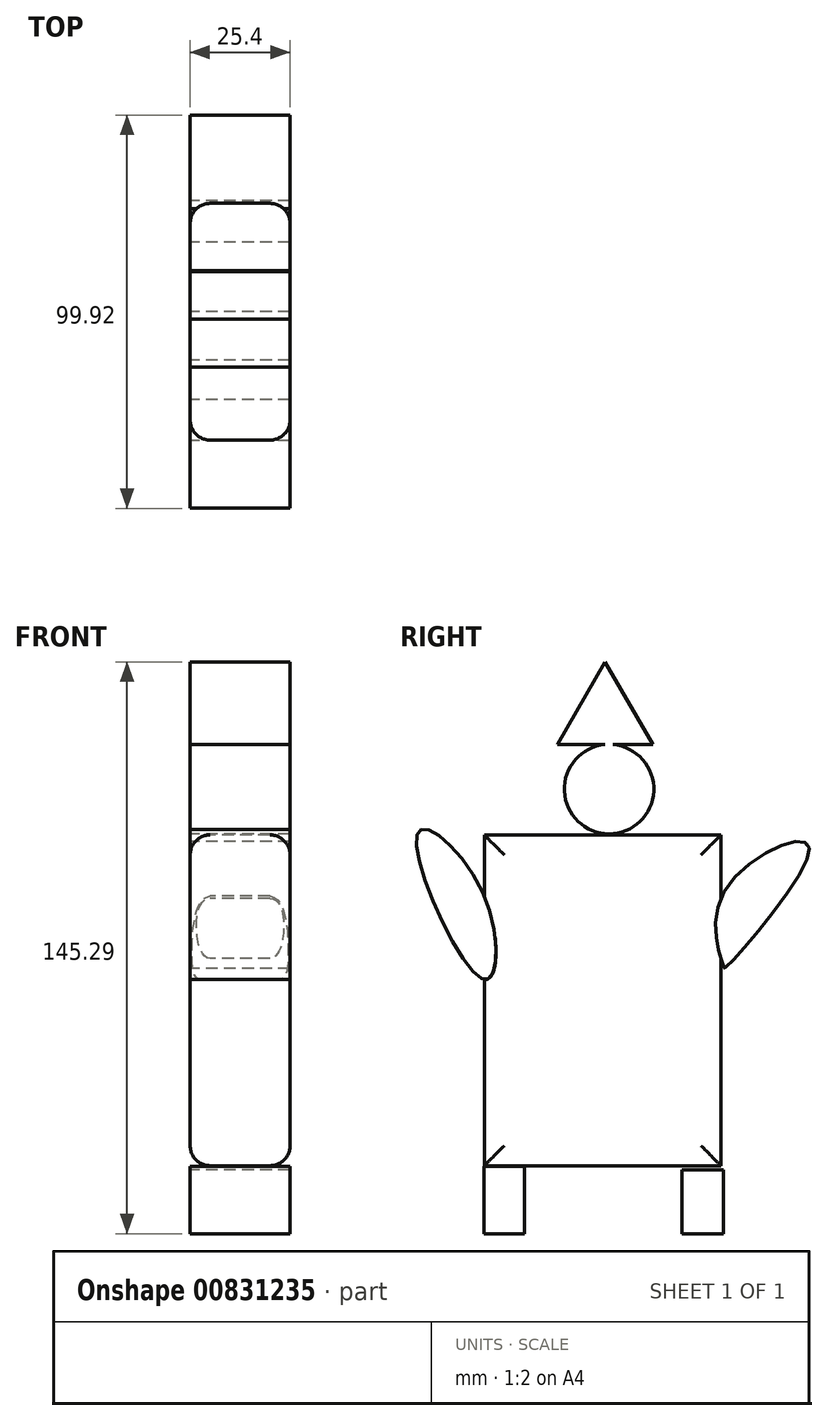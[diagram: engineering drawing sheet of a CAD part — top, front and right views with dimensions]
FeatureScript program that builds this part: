
annotation { "Feature Type Name" : "Feature", "Feature Type Description" : "" }
export const myFeature = defineFeature(function(context is Context, id is Id, definition is map)
    precondition{}
    {
        {
            var Q0;
            Q0=qCreatedBy(makeId("Right.planeOp"),FACE);
            var sketch = newSketch(context, id + "F0", { "sketchPlane" : qUnion([Q0])});
            skLineSegment(sketch, "E0.bottom", {"start": v(-28.86, 27.79) * mm, "end": v(31.28, 27.79) * mm});
            skLineSegment(sketch, "E0.top", {"start": v(-28.86, -56.25) * mm, "end": v(31.28, -56.25) * mm});
            skLineSegment(sketch, "E0.left", {"start": v(-28.86, 27.79) * mm, "end": v(-28.86, -56.25) * mm});
            skLineSegment(sketch, "E0.right", {"start": v(31.28, 27.79) * mm, "end": v(31.28, -56.25) * mm});
            skSolve(sketch);
        }
        {
            var Q0;
            Q0=makeQuery(id+"F0.imprint","IMPRINT",FACE,{"disambiguationData":[TD([[makeQuery(id+"F0.imprint","IMPRINT",EDGE,{"derivedFrom":sQuery(id+"F0.wireOp",EDGE,"E0.bottom")}),-1.0]])]});
            extrude(context, id + "F1", {"entities" : qUnion([Q0]), "depth" : 25.4 * mm, "offsetDistance" : 25.4 * mm});
        }
        {
            var Q0;
            Q0=makeQuery(id+"F1.opExtrude","CAP_EDGE",EDGE,{"disambiguationData":[OSD([sQuery(id+"F0.wireOp",EDGE,"E0.left")])],"isStart":false});
            var Q1;
            Q1=makeQuery(id+"F1.opExtrude","CAP_EDGE",EDGE,{"disambiguationData":[OSD([sQuery(id+"F0.wireOp",EDGE,"E0.right")])],"isStart":false});
            var Q2;
            Q2=makeQuery(id+"F1.opExtrude","CAP_EDGE",EDGE,{"disambiguationData":[OSD([sQuery(id+"F0.wireOp",EDGE,"E0.bottom")])],"isStart":false});
            var Q3;
            Q3=makeQuery(id+"F1.opExtrude","CAP_EDGE",EDGE,{"disambiguationData":[OSD([sQuery(id+"F0.wireOp",EDGE,"E0.top")])],"isStart":false});
            var Q4;
            Q4=makeQuery(id+"F1.opExtrude","CAP_EDGE",EDGE,{"disambiguationData":[OSD([sQuery(id+"F0.wireOp",EDGE,"E0.bottom")])],"isStart":true});
            var Q5;
            Q5=makeQuery(id+"F1.opExtrude","CAP_EDGE",EDGE,{"disambiguationData":[OSD([sQuery(id+"F0.wireOp",EDGE,"E0.top")])],"isStart":true});
            var Q6;
            Q6=makeQuery(id+"F1.opExtrude","CAP_EDGE",EDGE,{"disambiguationData":[OSD([sQuery(id+"F0.wireOp",EDGE,"E0.left")])],"isStart":true});
            var Q7;
            Q7=makeQuery(id+"F1.opExtrude","CAP_EDGE",EDGE,{"disambiguationData":[OSD([sQuery(id+"F0.wireOp",EDGE,"E0.right")])],"isStart":true});
            fillet(context, id + "F2", {"entities" : qUnion([Q0, Q1, Q2, Q3, Q4, Q5, Q6, Q7]), "radius" : 5.08 * mm, "tangentPropagation" : true, "allowEdgeOverflow" : false});
        }
        {
            var Q0;
            Q0=qCreatedBy(makeId("Right.planeOp"),FACE);
            var sketch = newSketch(context, id + "F3", { "sketchPlane" : qUnion([Q0])});
            skCircle(sketch, "E1", {"center": v(2.83, 39.42) * mm, "radius": 11.37 * mm});
            skPoint(sketch, "E1.first.point", {"position": v(1.83, 50.74) * mm});
            skPoint(sketch, "E1.second.point", {"position": v(3.31, 28.06) * mm});
            skPoint(sketch, "E1.third.point", {"position": v(11.42, 46.86) * mm});
            skFitSpline(sketch, "E2", {"points": [v(32.08, 13.3) * mm, v(53.66, 24.73) * mm, v(32.27, -6.06) * mm, v(32.09, -6.06) * mm, v(31.9, -5.5) * mm, v(32.08, 13.3) * mm]});
            skFitSpline(sketch, "E3", {"points": [v(-29.33, 13.3) * mm, v(-45.93, 28.07) * mm, v(-29.32, -8.81) * mm, v(-29.33, 13.3) * mm]});
            skLineSegment(sketch, "E4.bottom", {"start": v(-18.62, -56.38) * mm, "end": v(-28.94, -56.38) * mm});
            skLineSegment(sketch, "E4.top", {"start": v(-18.62, -73.53) * mm, "end": v(-28.94, -73.53) * mm});
            skLineSegment(sketch, "E4.left", {"start": v(-18.62, -56.38) * mm, "end": v(-18.62, -73.53) * mm});
            skLineSegment(sketch, "E4.right", {"start": v(-28.94, -56.38) * mm, "end": v(-28.94, -73.53) * mm});
            skLineSegment(sketch, "E5.bottom", {"start": v(31.92, -57.32) * mm, "end": v(21.4, -57.32) * mm});
            skLineSegment(sketch, "E5.top", {"start": v(31.92, -73.53) * mm, "end": v(21.4, -73.53) * mm});
            skLineSegment(sketch, "E5.left", {"start": v(31.92, -57.32) * mm, "end": v(31.92, -73.53) * mm});
            skLineSegment(sketch, "E5.right", {"start": v(21.4, -57.32) * mm, "end": v(21.4, -73.53) * mm});
            skCircle(sketch, "E6.cCircle", {"center": v(1.83, 57.74) * mm, "radius": 7 * mm, "construction": true});
            skLineSegment(sketch, "E6.0", {"start": v(13.96, 50.74) * mm, "end": v(-10.3, 50.73) * mm});
            skLineSegment(sketch, "E6.1", {"start": v(-10.3, 50.73) * mm, "end": v(1.82, 71.76) * mm});
            skLineSegment(sketch, "E6.2", {"start": v(1.82, 71.76) * mm, "end": v(13.96, 50.74) * mm});
            skCircle(sketch, "E7.cCircle", {"center": v(1.83, 50.74) * mm, "radius": 2 * mm, "construction": true});
            skLineSegment(sketch, "E7.0", {"start": v(3.83, 50.86) * mm, "end": v(3.83, 50.61) * mm, "construction": true});
            skLineSegment(sketch, "E7.1", {"start": v(3.83, 50.61) * mm, "end": v(3.8, 50.36) * mm, "construction": true});
            skLineSegment(sketch, "E7.2", {"start": v(3.8, 50.36) * mm, "end": v(3.74, 50.12) * mm, "construction": true});
            skLineSegment(sketch, "E7.3", {"start": v(3.74, 50.12) * mm, "end": v(3.65, 49.88) * mm, "construction": true});
            skLineSegment(sketch, "E7.4", {"start": v(3.65, 49.88) * mm, "end": v(3.52, 49.66) * mm, "construction": true});
            skLineSegment(sketch, "E7.5", {"start": v(3.52, 49.66) * mm, "end": v(3.38, 49.46) * mm, "construction": true});
            skLineSegment(sketch, "E7.6", {"start": v(3.38, 49.46) * mm, "end": v(3.2, 49.28) * mm, "construction": true});
            skLineSegment(sketch, "E7.7", {"start": v(3.2, 49.28) * mm, "end": v(3, 49.11) * mm, "construction": true});
            skLineSegment(sketch, "E7.8", {"start": v(3, 49.11) * mm, "end": v(2.8, 48.98) * mm, "construction": true});
            skLineSegment(sketch, "E7.9", {"start": v(2.8, 48.98) * mm, "end": v(2.57, 48.87) * mm, "construction": true});
            skLineSegment(sketch, "E7.10", {"start": v(2.57, 48.87) * mm, "end": v(2.33, 48.8) * mm, "construction": true});
            skLineSegment(sketch, "E7.11", {"start": v(2.33, 48.8) * mm, "end": v(2.08, 48.75) * mm, "construction": true});
            skLineSegment(sketch, "E7.12", {"start": v(2.08, 48.75) * mm, "end": v(1.83, 48.73) * mm, "construction": true});
            skLineSegment(sketch, "E7.13", {"start": v(1.83, 48.73) * mm, "end": v(1.58, 48.75) * mm, "construction": true});
            skLineSegment(sketch, "E7.14", {"start": v(1.58, 48.75) * mm, "end": v(1.33, 48.8) * mm, "construction": true});
            skLineSegment(sketch, "E7.15", {"start": v(1.33, 48.8) * mm, "end": v(1.1, 48.87) * mm, "construction": true});
            skLineSegment(sketch, "E7.16", {"start": v(1.1, 48.87) * mm, "end": v(0.86, 48.98) * mm, "construction": true});
            skLineSegment(sketch, "E7.17", {"start": v(0.86, 48.98) * mm, "end": v(0.65, 49.11) * mm, "construction": true});
            skLineSegment(sketch, "E7.18", {"start": v(0.65, 49.11) * mm, "end": v(0.46, 49.27) * mm, "construction": true});
            skLineSegment(sketch, "E7.19", {"start": v(0.46, 49.27) * mm, "end": v(0.28, 49.46) * mm, "construction": true});
            skLineSegment(sketch, "E7.20", {"start": v(0.28, 49.46) * mm, "end": v(0.14, 49.66) * mm, "construction": true});
            skLineSegment(sketch, "E7.21", {"start": v(0.14, 49.66) * mm, "end": v(0.01, 49.88) * mm, "construction": true});
            skLineSegment(sketch, "E7.22", {"start": v(0.01, 49.88) * mm, "end": v(-0.08, 50.12) * mm, "construction": true});
            skLineSegment(sketch, "E7.23", {"start": v(-0.08, 50.12) * mm, "end": v(-0.14, 50.36) * mm, "construction": true});
            skLineSegment(sketch, "E7.24", {"start": v(-0.14, 50.36) * mm, "end": v(-0.17, 50.61) * mm, "construction": true});
            skLineSegment(sketch, "E7.25", {"start": v(-0.17, 50.61) * mm, "end": v(-0.17, 50.86) * mm, "construction": true});
            skLineSegment(sketch, "E7.26", {"start": v(-0.17, 50.86) * mm, "end": v(-0.14, 51.11) * mm, "construction": true});
            skLineSegment(sketch, "E7.27", {"start": v(-0.14, 51.11) * mm, "end": v(-0.08, 51.36) * mm, "construction": true});
            skLineSegment(sketch, "E7.28", {"start": v(-0.08, 51.36) * mm, "end": v(0.01, 51.6) * mm, "construction": true});
            skLineSegment(sketch, "E7.29", {"start": v(0.01, 51.6) * mm, "end": v(0.13, 51.81) * mm, "construction": true});
            skLineSegment(sketch, "E7.30", {"start": v(0.13, 51.81) * mm, "end": v(0.28, 52.02) * mm, "construction": true});
            skLineSegment(sketch, "E7.31", {"start": v(0.28, 52.02) * mm, "end": v(0.46, 52.2) * mm, "construction": true});
            skLineSegment(sketch, "E7.32", {"start": v(0.46, 52.2) * mm, "end": v(0.65, 52.36) * mm, "construction": true});
            skLineSegment(sketch, "E7.33", {"start": v(0.65, 52.36) * mm, "end": v(0.86, 52.5) * mm, "construction": true});
            skLineSegment(sketch, "E7.34", {"start": v(0.86, 52.5) * mm, "end": v(1.1, 52.6) * mm, "construction": true});
            skLineSegment(sketch, "E7.35", {"start": v(1.1, 52.6) * mm, "end": v(1.33, 52.68) * mm, "construction": true});
            skLineSegment(sketch, "E7.36", {"start": v(1.33, 52.68) * mm, "end": v(1.58, 52.73) * mm, "construction": true});
            skLineSegment(sketch, "E7.37", {"start": v(1.58, 52.73) * mm, "end": v(1.83, 52.74) * mm, "construction": true});
            skLineSegment(sketch, "E7.38", {"start": v(1.83, 52.74) * mm, "end": v(2.08, 52.73) * mm, "construction": true});
            skLineSegment(sketch, "E7.39", {"start": v(2.08, 52.73) * mm, "end": v(2.33, 52.68) * mm, "construction": true});
            skLineSegment(sketch, "E7.40", {"start": v(2.33, 52.68) * mm, "end": v(2.57, 52.6) * mm, "construction": true});
            skLineSegment(sketch, "E7.41", {"start": v(2.57, 52.6) * mm, "end": v(2.8, 52.5) * mm, "construction": true});
            skLineSegment(sketch, "E7.42", {"start": v(2.8, 52.5) * mm, "end": v(3, 52.36) * mm, "construction": true});
            skLineSegment(sketch, "E7.43", {"start": v(3, 52.36) * mm, "end": v(3.2, 52.2) * mm, "construction": true});
            skLineSegment(sketch, "E7.44", {"start": v(3.2, 52.2) * mm, "end": v(3.37, 52.02) * mm, "construction": true});
            skLineSegment(sketch, "E7.45", {"start": v(3.37, 52.02) * mm, "end": v(3.52, 51.81) * mm, "construction": true});
            skLineSegment(sketch, "E7.46", {"start": v(3.52, 51.81) * mm, "end": v(3.64, 51.6) * mm, "construction": true});
            skLineSegment(sketch, "E7.47", {"start": v(3.64, 51.6) * mm, "end": v(3.74, 51.36) * mm, "construction": true});
            skLineSegment(sketch, "E7.48", {"start": v(3.74, 51.36) * mm, "end": v(3.8, 51.11) * mm, "construction": true});
            skLineSegment(sketch, "E7.49", {"start": v(3.8, 51.11) * mm, "end": v(3.83, 50.86) * mm, "construction": true});
            skPoint(sketch, "E7.0.midPoint", {"position": v(3.83, 50.74) * mm});
            skCircle(sketch, "E8.cCircle", {"center": v(32.08, 13.3) * mm, "radius": 18.8 * mm, "construction": true});
            skLineSegment(sketch, "E8.0", {"start": v(33.09, -5.52) * mm, "end": v(30.72, -5.5) * mm, "construction": true});
            skLineSegment(sketch, "E8.1", {"start": v(30.72, -5.5) * mm, "end": v(28.38, -5.18) * mm, "construction": true});
            skLineSegment(sketch, "E8.2", {"start": v(28.38, -5.18) * mm, "end": v(26.09, -4.57) * mm, "construction": true});
            skLineSegment(sketch, "E8.3", {"start": v(26.09, -4.57) * mm, "end": v(23.9, -3.67) * mm, "construction": true});
            skLineSegment(sketch, "E8.4", {"start": v(23.9, -3.67) * mm, "end": v(21.83, -2.51) * mm, "construction": true});
            skLineSegment(sketch, "E8.5", {"start": v(21.83, -2.51) * mm, "end": v(19.93, -1.1) * mm, "construction": true});
            skLineSegment(sketch, "E8.6", {"start": v(19.93, -1.1) * mm, "end": v(18.22, 0.53) * mm, "construction": true});
            skLineSegment(sketch, "E8.7", {"start": v(18.22, 0.53) * mm, "end": v(16.73, 2.37) * mm, "construction": true});
            skLineSegment(sketch, "E8.8", {"start": v(16.73, 2.37) * mm, "end": v(15.48, 4.38) * mm, "construction": true});
            skLineSegment(sketch, "E8.9", {"start": v(15.48, 4.38) * mm, "end": v(14.5, 6.53) * mm, "construction": true});
            skLineSegment(sketch, "E8.10", {"start": v(14.5, 6.53) * mm, "end": v(13.79, 8.79) * mm, "construction": true});
            skLineSegment(sketch, "E8.11", {"start": v(13.79, 8.79) * mm, "end": v(13.36, 11.12) * mm, "construction": true});
            skLineSegment(sketch, "E8.12", {"start": v(13.36, 11.12) * mm, "end": v(13.24, 13.48) * mm, "construction": true});
            skLineSegment(sketch, "E8.13", {"start": v(13.24, 13.48) * mm, "end": v(13.41, 15.84) * mm, "construction": true});
            skLineSegment(sketch, "E8.14", {"start": v(13.41, 15.84) * mm, "end": v(13.88, 18.16) * mm, "construction": true});
            skLineSegment(sketch, "E8.15", {"start": v(13.88, 18.16) * mm, "end": v(14.63, 20.4) * mm, "construction": true});
            skLineSegment(sketch, "E8.16", {"start": v(14.63, 20.4) * mm, "end": v(15.66, 22.54) * mm, "construction": true});
            skLineSegment(sketch, "E8.17", {"start": v(15.66, 22.54) * mm, "end": v(16.94, 24.52) * mm, "construction": true});
            skLineSegment(sketch, "E8.18", {"start": v(16.94, 24.52) * mm, "end": v(18.47, 26.33) * mm, "construction": true});
            skLineSegment(sketch, "E8.19", {"start": v(18.47, 26.33) * mm, "end": v(20.21, 27.94) * mm, "construction": true});
            skLineSegment(sketch, "E8.20", {"start": v(20.21, 27.94) * mm, "end": v(22.14, 29.3) * mm, "construction": true});
            skLineSegment(sketch, "E8.21", {"start": v(22.14, 29.3) * mm, "end": v(24.22, 30.43) * mm, "construction": true});
            skLineSegment(sketch, "E8.22", {"start": v(24.22, 30.43) * mm, "end": v(26.43, 31.28) * mm, "construction": true});
            skLineSegment(sketch, "E8.23", {"start": v(26.43, 31.28) * mm, "end": v(28.73, 31.84) * mm, "construction": true});
            skLineSegment(sketch, "E8.24", {"start": v(28.73, 31.84) * mm, "end": v(31.08, 32.12) * mm, "construction": true});
            skLineSegment(sketch, "E8.25", {"start": v(31.08, 32.12) * mm, "end": v(33.45, 32.1) * mm, "construction": true});
            skLineSegment(sketch, "E8.26", {"start": v(33.45, 32.1) * mm, "end": v(35.8, 31.78) * mm, "construction": true});
            skLineSegment(sketch, "E8.27", {"start": v(35.8, 31.78) * mm, "end": v(38.08, 31.17) * mm, "construction": true});
            skLineSegment(sketch, "E8.28", {"start": v(38.08, 31.17) * mm, "end": v(40.27, 30.27) * mm, "construction": true});
            skLineSegment(sketch, "E8.29", {"start": v(40.27, 30.27) * mm, "end": v(42.33, 29.11) * mm, "construction": true});
            skLineSegment(sketch, "E8.30", {"start": v(42.33, 29.11) * mm, "end": v(44.23, 27.7) * mm, "construction": true});
            skLineSegment(sketch, "E8.31", {"start": v(44.23, 27.7) * mm, "end": v(45.94, 26.07) * mm, "construction": true});
            skLineSegment(sketch, "E8.32", {"start": v(45.94, 26.07) * mm, "end": v(47.43, 24.23) * mm, "construction": true});
            skLineSegment(sketch, "E8.33", {"start": v(47.43, 24.23) * mm, "end": v(48.68, 22.22) * mm, "construction": true});
            skLineSegment(sketch, "E8.34", {"start": v(48.68, 22.22) * mm, "end": v(49.67, 20.07) * mm, "construction": true});
            skLineSegment(sketch, "E8.35", {"start": v(49.67, 20.07) * mm, "end": v(50.38, 17.81) * mm, "construction": true});
            skLineSegment(sketch, "E8.36", {"start": v(50.38, 17.81) * mm, "end": v(50.8, 15.48) * mm, "construction": true});
            skLineSegment(sketch, "E8.37", {"start": v(50.8, 15.48) * mm, "end": v(50.93, 13.12) * mm, "construction": true});
            skLineSegment(sketch, "E8.38", {"start": v(50.93, 13.12) * mm, "end": v(50.76, 10.76) * mm, "construction": true});
            skLineSegment(sketch, "E8.39", {"start": v(50.76, 10.76) * mm, "end": v(50.3, 8.44) * mm, "construction": true});
            skLineSegment(sketch, "E8.40", {"start": v(50.3, 8.44) * mm, "end": v(49.54, 6.2) * mm, "construction": true});
            skLineSegment(sketch, "E8.41", {"start": v(49.54, 6.2) * mm, "end": v(48.5, 4.06) * mm, "construction": true});
            skLineSegment(sketch, "E8.42", {"start": v(48.5, 4.06) * mm, "end": v(47.22, 2.08) * mm, "construction": true});
            skLineSegment(sketch, "E8.43", {"start": v(47.22, 2.08) * mm, "end": v(45.7, 0.27) * mm, "construction": true});
            skLineSegment(sketch, "E8.44", {"start": v(45.7, 0.27) * mm, "end": v(43.96, -1.33) * mm, "construction": true});
            skLineSegment(sketch, "E8.45", {"start": v(43.96, -1.33) * mm, "end": v(42.03, -2.7) * mm, "construction": true});
            skLineSegment(sketch, "E8.46", {"start": v(42.03, -2.7) * mm, "end": v(39.94, -3.83) * mm, "construction": true});
            skLineSegment(sketch, "E8.47", {"start": v(39.94, -3.83) * mm, "end": v(37.74, -4.68) * mm, "construction": true});
            skLineSegment(sketch, "E8.48", {"start": v(37.74, -4.68) * mm, "end": v(35.44, -5.24) * mm, "construction": true});
            skLineSegment(sketch, "E8.49", {"start": v(35.44, -5.24) * mm, "end": v(33.09, -5.52) * mm, "construction": true});
            skCircle(sketch, "E9.cCircle", {"center": v(-29.32, -8.81) * mm, "radius": 22.11 * mm, "construction": true});
            skLineSegment(sketch, "E9.0", {"start": v(-30.72, 13.3) * mm, "end": v(-27.94, 13.3) * mm, "construction": true});
            skLineSegment(sketch, "E9.1", {"start": v(-27.94, 13.3) * mm, "end": v(-25.18, 12.95) * mm, "construction": true});
            skLineSegment(sketch, "E9.2", {"start": v(-25.18, 12.95) * mm, "end": v(-22.48, 12.26) * mm, "construction": true});
            skLineSegment(sketch, "E9.3", {"start": v(-22.48, 12.26) * mm, "end": v(-19.9, 11.24) * mm, "construction": true});
            skLineSegment(sketch, "E9.4", {"start": v(-19.9, 11.24) * mm, "end": v(-17.46, 9.9) * mm, "construction": true});
            skLineSegment(sketch, "E9.5", {"start": v(-17.46, 9.9) * mm, "end": v(-15.2, 8.26) * mm, "construction": true});
            skLineSegment(sketch, "E9.6", {"start": v(-15.2, 8.26) * mm, "end": v(-13.18, 6.36) * mm, "construction": true});
            skLineSegment(sketch, "E9.7", {"start": v(-13.18, 6.36) * mm, "end": v(-11.4, 4.22) * mm, "construction": true});
            skLineSegment(sketch, "E9.8", {"start": v(-11.4, 4.22) * mm, "end": v(-9.91, 1.87) * mm, "construction": true});
            skLineSegment(sketch, "E9.9", {"start": v(-9.91, 1.87) * mm, "end": v(-8.73, -0.65) * mm, "construction": true});
            skLineSegment(sketch, "E9.10", {"start": v(-8.73, -0.65) * mm, "end": v(-7.87, -3.3) * mm, "construction": true});
            skLineSegment(sketch, "E9.11", {"start": v(-7.87, -3.3) * mm, "end": v(-7.34, -6.03) * mm, "construction": true});
            skLineSegment(sketch, "E9.12", {"start": v(-7.34, -6.03) * mm, "end": v(-7.17, -8.8) * mm, "construction": true});
            skLineSegment(sketch, "E9.13", {"start": v(-7.17, -8.8) * mm, "end": v(-7.34, -11.58) * mm, "construction": true});
            skLineSegment(sketch, "E9.14", {"start": v(-7.34, -11.58) * mm, "end": v(-7.86, -14.32) * mm, "construction": true});
            skLineSegment(sketch, "E9.15", {"start": v(-7.86, -14.32) * mm, "end": v(-8.72, -16.96) * mm, "construction": true});
            skLineSegment(sketch, "E9.16", {"start": v(-8.72, -16.96) * mm, "end": v(-9.9, -19.48) * mm, "construction": true});
            skLineSegment(sketch, "E9.17", {"start": v(-9.9, -19.48) * mm, "end": v(-11.4, -21.83) * mm, "construction": true});
            skLineSegment(sketch, "E9.18", {"start": v(-11.4, -21.83) * mm, "end": v(-13.17, -23.97) * mm, "construction": true});
            skLineSegment(sketch, "E9.19", {"start": v(-13.17, -23.97) * mm, "end": v(-15.2, -25.88) * mm, "construction": true});
            skLineSegment(sketch, "E9.20", {"start": v(-15.2, -25.88) * mm, "end": v(-17.45, -27.51) * mm, "construction": true});
            skLineSegment(sketch, "E9.21", {"start": v(-17.45, -27.51) * mm, "end": v(-19.89, -28.86) * mm, "construction": true});
            skLineSegment(sketch, "E9.22", {"start": v(-19.89, -28.86) * mm, "end": v(-22.47, -29.88) * mm, "construction": true});
            skLineSegment(sketch, "E9.23", {"start": v(-22.47, -29.88) * mm, "end": v(-25.17, -30.57) * mm, "construction": true});
            skLineSegment(sketch, "E9.24", {"start": v(-25.17, -30.57) * mm, "end": v(-27.93, -30.92) * mm, "construction": true});
            skLineSegment(sketch, "E9.25", {"start": v(-27.93, -30.92) * mm, "end": v(-30.7, -30.92) * mm, "construction": true});
            skLineSegment(sketch, "E9.26", {"start": v(-30.7, -30.92) * mm, "end": v(-33.47, -30.57) * mm, "construction": true});
            skLineSegment(sketch, "E9.27", {"start": v(-33.47, -30.57) * mm, "end": v(-36.17, -29.88) * mm, "construction": true});
            skLineSegment(sketch, "E9.28", {"start": v(-36.17, -29.88) * mm, "end": v(-38.75, -28.86) * mm, "construction": true});
            skLineSegment(sketch, "E9.29", {"start": v(-38.75, -28.86) * mm, "end": v(-41.2, -27.52) * mm, "construction": true});
            skLineSegment(sketch, "E9.30", {"start": v(-41.2, -27.52) * mm, "end": v(-43.44, -25.88) * mm, "construction": true});
            skLineSegment(sketch, "E9.31", {"start": v(-43.44, -25.88) * mm, "end": v(-45.47, -23.98) * mm, "construction": true});
            skLineSegment(sketch, "E9.32", {"start": v(-45.47, -23.98) * mm, "end": v(-47.24, -21.84) * mm, "construction": true});
            skLineSegment(sketch, "E9.33", {"start": v(-47.24, -21.84) * mm, "end": v(-48.74, -19.49) * mm, "construction": true});
            skLineSegment(sketch, "E9.34", {"start": v(-48.74, -19.49) * mm, "end": v(-49.92, -16.97) * mm, "construction": true});
            skLineSegment(sketch, "E9.35", {"start": v(-49.92, -16.97) * mm, "end": v(-50.78, -14.33) * mm, "construction": true});
            skLineSegment(sketch, "E9.36", {"start": v(-50.78, -14.33) * mm, "end": v(-51.3, -11.6) * mm, "construction": true});
            skLineSegment(sketch, "E9.37", {"start": v(-51.3, -11.6) * mm, "end": v(-51.48, -8.82) * mm, "construction": true});
            skLineSegment(sketch, "E9.38", {"start": v(-51.48, -8.82) * mm, "end": v(-51.3, -6.04) * mm, "construction": true});
            skLineSegment(sketch, "E9.39", {"start": v(-51.3, -6.04) * mm, "end": v(-50.78, -3.3) * mm, "construction": true});
            skLineSegment(sketch, "E9.40", {"start": v(-50.78, -3.3) * mm, "end": v(-49.92, -0.66) * mm, "construction": true});
            skLineSegment(sketch, "E9.41", {"start": v(-49.92, -0.66) * mm, "end": v(-48.74, 1.86) * mm, "construction": true});
            skLineSegment(sketch, "E9.42", {"start": v(-48.74, 1.86) * mm, "end": v(-47.25, 4.2) * mm, "construction": true});
            skLineSegment(sketch, "E9.43", {"start": v(-47.25, 4.2) * mm, "end": v(-45.48, 6.35) * mm, "construction": true});
            skLineSegment(sketch, "E9.44", {"start": v(-45.48, 6.35) * mm, "end": v(-43.45, 8.26) * mm, "construction": true});
            skLineSegment(sketch, "E9.45", {"start": v(-43.45, 8.26) * mm, "end": v(-41.2, 9.9) * mm, "construction": true});
            skLineSegment(sketch, "E9.46", {"start": v(-41.2, 9.9) * mm, "end": v(-38.76, 11.23) * mm, "construction": true});
            skLineSegment(sketch, "E9.47", {"start": v(-38.76, 11.23) * mm, "end": v(-36.17, 12.26) * mm, "construction": true});
            skLineSegment(sketch, "E9.48", {"start": v(-36.17, 12.26) * mm, "end": v(-33.48, 12.95) * mm, "construction": true});
            skLineSegment(sketch, "E9.49", {"start": v(-33.48, 12.95) * mm, "end": v(-30.72, 13.3) * mm, "construction": true});
            skCircle(sketch, "E10.cCircle", {"center": v(-18.62, -56.38) * mm, "radius": 10.32 * mm, "construction": true});
            skLineSegment(sketch, "E10.0", {"start": v(-28.94, -57.03) * mm, "end": v(-28.94, -55.73) * mm, "construction": true});
            skLineSegment(sketch, "E10.1", {"start": v(-28.94, -55.73) * mm, "end": v(-28.78, -54.45) * mm, "construction": true});
            skLineSegment(sketch, "E10.2", {"start": v(-28.78, -54.45) * mm, "end": v(-28.45, -53.19) * mm, "construction": true});
            skLineSegment(sketch, "E10.3", {"start": v(-28.45, -53.19) * mm, "end": v(-27.98, -51.98) * mm, "construction": true});
            skLineSegment(sketch, "E10.4", {"start": v(-27.98, -51.98) * mm, "end": v(-27.35, -50.84) * mm, "construction": true});
            skLineSegment(sketch, "E10.5", {"start": v(-27.35, -50.84) * mm, "end": v(-26.59, -49.8) * mm, "construction": true});
            skLineSegment(sketch, "E10.6", {"start": v(-26.59, -49.8) * mm, "end": v(-25.7, -48.84) * mm, "construction": true});
            skLineSegment(sketch, "E10.7", {"start": v(-25.7, -48.84) * mm, "end": v(-24.7, -48.02) * mm, "construction": true});
            skLineSegment(sketch, "E10.8", {"start": v(-24.7, -48.02) * mm, "end": v(-23.6, -47.32) * mm, "construction": true});
            skLineSegment(sketch, "E10.9", {"start": v(-23.6, -47.32) * mm, "end": v(-22.42, -46.77) * mm, "construction": true});
            skLineSegment(sketch, "E10.10", {"start": v(-22.42, -46.77) * mm, "end": v(-21.19, -46.37) * mm, "construction": true});
            skLineSegment(sketch, "E10.11", {"start": v(-21.19, -46.37) * mm, "end": v(-19.91, -46.12) * mm, "construction": true});
            skLineSegment(sketch, "E10.12", {"start": v(-19.91, -46.12) * mm, "end": v(-18.62, -46.04) * mm, "construction": true});
            skLineSegment(sketch, "E10.13", {"start": v(-18.62, -46.04) * mm, "end": v(-17.32, -46.12) * mm, "construction": true});
            skLineSegment(sketch, "E10.14", {"start": v(-17.32, -46.12) * mm, "end": v(-16.04, -46.37) * mm, "construction": true});
            skLineSegment(sketch, "E10.15", {"start": v(-16.04, -46.37) * mm, "end": v(-14.8, -46.77) * mm, "construction": true});
            skLineSegment(sketch, "E10.16", {"start": v(-14.8, -46.77) * mm, "end": v(-13.63, -47.32) * mm, "construction": true});
            skLineSegment(sketch, "E10.17", {"start": v(-13.63, -47.32) * mm, "end": v(-12.54, -48.02) * mm, "construction": true});
            skLineSegment(sketch, "E10.18", {"start": v(-12.54, -48.02) * mm, "end": v(-11.53, -48.84) * mm, "construction": true});
            skLineSegment(sketch, "E10.19", {"start": v(-11.53, -48.84) * mm, "end": v(-10.65, -49.8) * mm, "construction": true});
            skLineSegment(sketch, "E10.20", {"start": v(-10.65, -49.8) * mm, "end": v(-9.88, -50.84) * mm, "construction": true});
            skLineSegment(sketch, "E10.21", {"start": v(-9.88, -50.84) * mm, "end": v(-9.26, -51.98) * mm, "construction": true});
            skLineSegment(sketch, "E10.22", {"start": v(-9.26, -51.98) * mm, "end": v(-8.78, -53.19) * mm, "construction": true});
            skLineSegment(sketch, "E10.23", {"start": v(-8.78, -53.19) * mm, "end": v(-8.46, -54.45) * mm, "construction": true});
            skLineSegment(sketch, "E10.24", {"start": v(-8.46, -54.45) * mm, "end": v(-8.3, -55.73) * mm, "construction": true});
            skLineSegment(sketch, "E10.25", {"start": v(-8.3, -55.73) * mm, "end": v(-8.3, -57.03) * mm, "construction": true});
            skLineSegment(sketch, "E10.26", {"start": v(-8.3, -57.03) * mm, "end": v(-8.46, -58.32) * mm, "construction": true});
            skLineSegment(sketch, "E10.27", {"start": v(-8.46, -58.32) * mm, "end": v(-8.78, -59.58) * mm, "construction": true});
            skLineSegment(sketch, "E10.28", {"start": v(-8.78, -59.58) * mm, "end": v(-9.26, -60.79) * mm, "construction": true});
            skLineSegment(sketch, "E10.29", {"start": v(-9.26, -60.79) * mm, "end": v(-9.88, -61.93) * mm, "construction": true});
            skLineSegment(sketch, "E10.30", {"start": v(-9.88, -61.93) * mm, "end": v(-10.65, -62.98) * mm, "construction": true});
            skLineSegment(sketch, "E10.31", {"start": v(-10.65, -62.98) * mm, "end": v(-11.53, -63.92) * mm, "construction": true});
            skLineSegment(sketch, "E10.32", {"start": v(-11.53, -63.92) * mm, "end": v(-12.54, -64.75) * mm, "construction": true});
            skLineSegment(sketch, "E10.33", {"start": v(-12.54, -64.75) * mm, "end": v(-13.63, -65.45) * mm, "construction": true});
            skLineSegment(sketch, "E10.34", {"start": v(-13.63, -65.45) * mm, "end": v(-14.8, -66) * mm, "construction": true});
            skLineSegment(sketch, "E10.35", {"start": v(-14.8, -66) * mm, "end": v(-16.04, -66.4) * mm, "construction": true});
            skLineSegment(sketch, "E10.36", {"start": v(-16.04, -66.4) * mm, "end": v(-17.32, -66.65) * mm, "construction": true});
            skLineSegment(sketch, "E10.37", {"start": v(-17.32, -66.65) * mm, "end": v(-18.62, -66.73) * mm, "construction": true});
            skLineSegment(sketch, "E10.38", {"start": v(-18.62, -66.73) * mm, "end": v(-19.91, -66.65) * mm, "construction": true});
            skLineSegment(sketch, "E10.39", {"start": v(-19.91, -66.65) * mm, "end": v(-21.19, -66.4) * mm, "construction": true});
            skLineSegment(sketch, "E10.40", {"start": v(-21.19, -66.4) * mm, "end": v(-22.42, -66) * mm, "construction": true});
            skLineSegment(sketch, "E10.41", {"start": v(-22.42, -66) * mm, "end": v(-23.6, -65.45) * mm, "construction": true});
            skLineSegment(sketch, "E10.42", {"start": v(-23.6, -65.45) * mm, "end": v(-24.7, -64.75) * mm, "construction": true});
            skLineSegment(sketch, "E10.43", {"start": v(-24.7, -64.75) * mm, "end": v(-25.7, -63.92) * mm, "construction": true});
            skLineSegment(sketch, "E10.44", {"start": v(-25.7, -63.92) * mm, "end": v(-26.59, -62.98) * mm, "construction": true});
            skLineSegment(sketch, "E10.45", {"start": v(-26.59, -62.98) * mm, "end": v(-27.35, -61.93) * mm, "construction": true});
            skLineSegment(sketch, "E10.46", {"start": v(-27.35, -61.93) * mm, "end": v(-27.98, -60.79) * mm, "construction": true});
            skLineSegment(sketch, "E10.47", {"start": v(-27.98, -60.79) * mm, "end": v(-28.45, -59.58) * mm, "construction": true});
            skLineSegment(sketch, "E10.48", {"start": v(-28.45, -59.58) * mm, "end": v(-28.78, -58.32) * mm, "construction": true});
            skLineSegment(sketch, "E10.49", {"start": v(-28.78, -58.32) * mm, "end": v(-28.94, -57.03) * mm, "construction": true});
            skPoint(sketch, "E10.0.midPoint", {"position": v(-28.94, -56.38) * mm});
            skCircle(sketch, "E11.cCircle", {"center": v(31.92, -57.32) * mm, "radius": 10.5 * mm, "construction": true});
            skLineSegment(sketch, "E11.0", {"start": v(21.4, -58.5) * mm, "end": v(21.4, -56.13) * mm, "construction": true});
            skLineSegment(sketch, "E11.1", {"start": v(21.4, -56.13) * mm, "end": v(21.93, -53.83) * mm, "construction": true});
            skLineSegment(sketch, "E11.2", {"start": v(21.93, -53.83) * mm, "end": v(22.96, -51.7) * mm, "construction": true});
            skLineSegment(sketch, "E11.3", {"start": v(22.96, -51.7) * mm, "end": v(24.44, -49.84) * mm, "construction": true});
            skLineSegment(sketch, "E11.4", {"start": v(24.44, -49.84) * mm, "end": v(26.29, -48.36) * mm, "construction": true});
            skLineSegment(sketch, "E11.5", {"start": v(26.29, -48.36) * mm, "end": v(28.42, -47.34) * mm, "construction": true});
            skLineSegment(sketch, "E11.6", {"start": v(28.42, -47.34) * mm, "end": v(30.73, -46.81) * mm, "construction": true});
            skLineSegment(sketch, "E11.7", {"start": v(30.73, -46.81) * mm, "end": v(33.1, -46.81) * mm, "construction": true});
            skLineSegment(sketch, "E11.8", {"start": v(33.1, -46.81) * mm, "end": v(35.4, -47.34) * mm, "construction": true});
            skLineSegment(sketch, "E11.9", {"start": v(35.4, -47.34) * mm, "end": v(37.54, -48.36) * mm, "construction": true});
            skLineSegment(sketch, "E11.10", {"start": v(37.54, -48.36) * mm, "end": v(39.4, -49.84) * mm, "construction": true});
            skLineSegment(sketch, "E11.11", {"start": v(39.4, -49.84) * mm, "end": v(40.87, -51.7) * mm, "construction": true});
            skLineSegment(sketch, "E11.12", {"start": v(40.87, -51.7) * mm, "end": v(41.9, -53.83) * mm, "construction": true});
            skLineSegment(sketch, "E11.13", {"start": v(41.9, -53.83) * mm, "end": v(42.42, -56.13) * mm, "construction": true});
            skLineSegment(sketch, "E11.14", {"start": v(42.42, -56.13) * mm, "end": v(42.42, -58.5) * mm, "construction": true});
            skLineSegment(sketch, "E11.15", {"start": v(42.42, -58.5) * mm, "end": v(41.9, -60.81) * mm, "construction": true});
            skLineSegment(sketch, "E11.16", {"start": v(41.9, -60.81) * mm, "end": v(40.87, -62.94) * mm, "construction": true});
            skLineSegment(sketch, "E11.17", {"start": v(40.87, -62.94) * mm, "end": v(39.4, -64.8) * mm, "construction": true});
            skLineSegment(sketch, "E11.18", {"start": v(39.4, -64.8) * mm, "end": v(37.54, -66.27) * mm, "construction": true});
            skLineSegment(sketch, "E11.19", {"start": v(37.54, -66.27) * mm, "end": v(35.4, -67.3) * mm, "construction": true});
            skLineSegment(sketch, "E11.20", {"start": v(35.4, -67.3) * mm, "end": v(33.1, -67.83) * mm, "construction": true});
            skLineSegment(sketch, "E11.21", {"start": v(33.1, -67.83) * mm, "end": v(30.73, -67.83) * mm, "construction": true});
            skLineSegment(sketch, "E11.22", {"start": v(30.73, -67.83) * mm, "end": v(28.42, -67.3) * mm, "construction": true});
            skLineSegment(sketch, "E11.23", {"start": v(28.42, -67.3) * mm, "end": v(26.29, -66.27) * mm, "construction": true});
            skLineSegment(sketch, "E11.24", {"start": v(26.29, -66.27) * mm, "end": v(24.44, -64.8) * mm, "construction": true});
            skLineSegment(sketch, "E11.25", {"start": v(24.44, -64.8) * mm, "end": v(22.96, -62.94) * mm, "construction": true});
            skLineSegment(sketch, "E11.26", {"start": v(22.96, -62.94) * mm, "end": v(21.93, -60.81) * mm, "construction": true});
            skLineSegment(sketch, "E11.27", {"start": v(21.93, -60.81) * mm, "end": v(21.4, -58.5) * mm, "construction": true});
            skPoint(sketch, "E11.0.midPoint", {"position": v(21.4, -57.32) * mm});
            skSolve(sketch);
        }
        {
            var Q0;
            Q0 = qSketchRegion(id + "F3", true);
            extrude(context, id + "F4", {"entities" : qUnion([Q0]), "operationType" : NewBodyOperationType.ADD, "depth" : 25.4 * mm, "offsetDistance" : 25.4 * mm});
        }
    });
